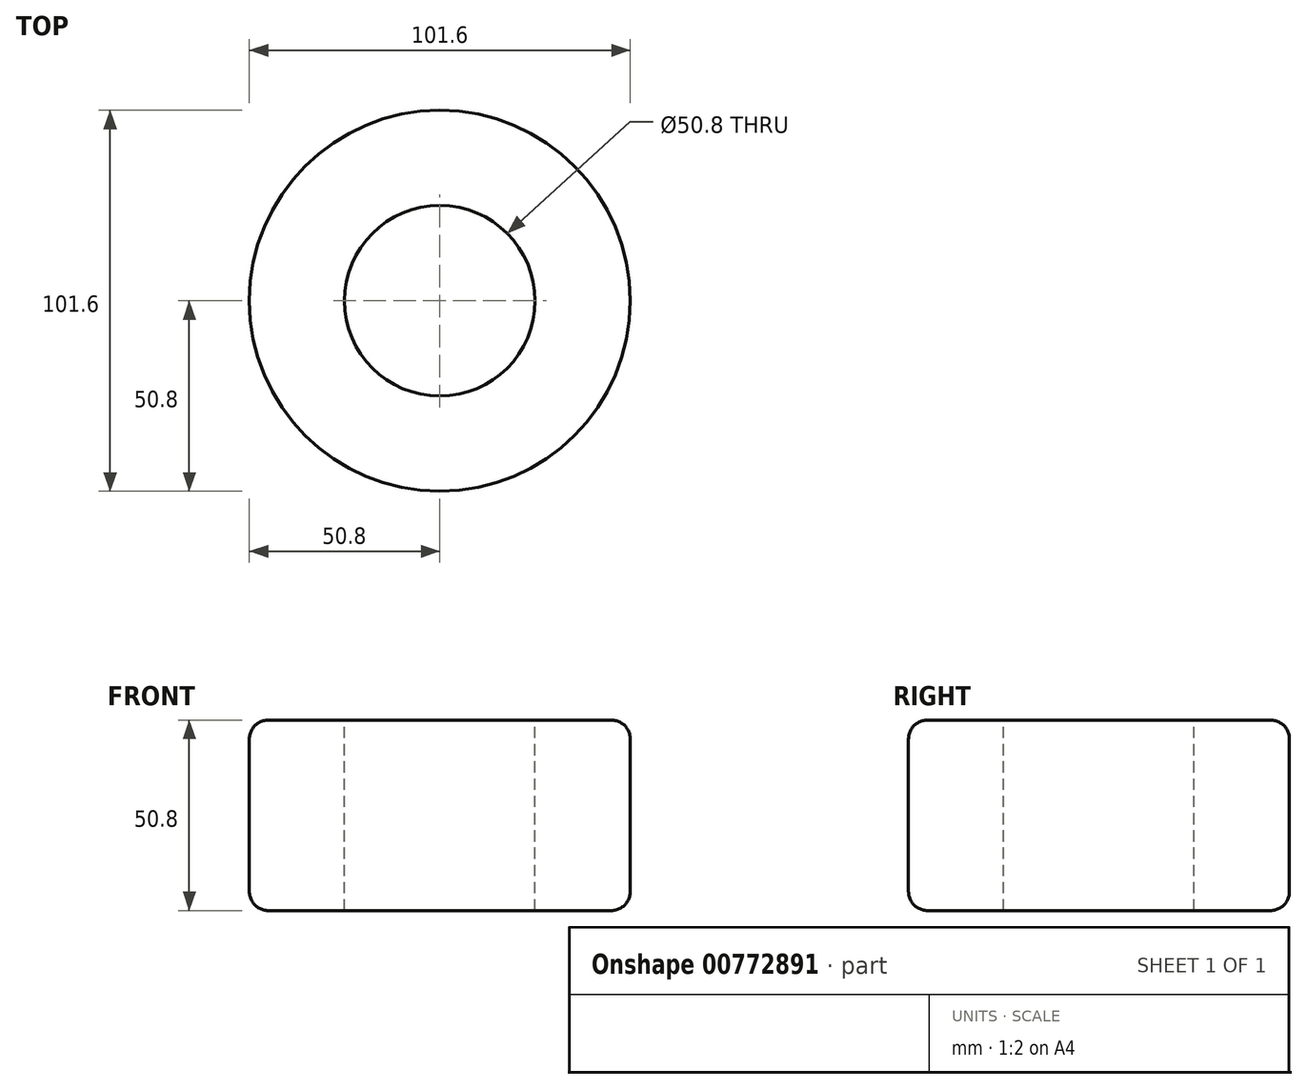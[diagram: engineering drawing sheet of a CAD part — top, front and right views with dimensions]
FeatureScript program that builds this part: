
annotation { "Feature Type Name" : "Feature", "Feature Type Description" : "" }
export const myFeature = defineFeature(function(context is Context, id is Id, definition is map)
    precondition{}
    {
        {
            var Q0;
            Q0=qCreatedBy(makeId("Top.planeOp"),FACE);
            var sketch = newSketch(context, id + "F0", { "sketchPlane" : qUnion([Q0])});
            skCircle(sketch, "E0", {"center": v(0, 0) * mm, "radius": 50.8 * mm});
            skSolve(sketch);
        }
        {
            var Q0;
            Q0=makeQuery(id+"F0.imprint","IMPRINT",FACE,{"disambiguationData":[TD([[makeQuery(id+"F0.imprint","IMPRINT",EDGE,{"derivedFrom":sQuery(id+"F0.wireOp",EDGE,"E0")}),1.0]])]});
            extrude(context, id + "F1", {"entities" : qUnion([Q0]), "oppositeDirection" : true, "depth" : 50.8 * mm, "offsetDistance" : 25.4 * mm});
        }
        {
            var Q0;
            Q0=qCreatedBy(makeId("Top.planeOp"),FACE);
            var sketch = newSketch(context, id + "F2", { "sketchPlane" : qUnion([Q0])});
            skCircle(sketch, "E1", {"center": v(0, 0) * mm, "radius": 25.4 * mm});
            skSolve(sketch);
        }
        {
            var Q0;
            Q0=makeQuery(id+"F2.imprint","IMPRINT",FACE,{"disambiguationData":[TD([[makeQuery(id+"F2.imprint","IMPRINT",EDGE,{"derivedFrom":sQuery(id+"F2.wireOp",EDGE,"E1")}),1.0]])]});
            extrude(context, id + "F3", {"entities" : qUnion([Q0]), "operationType" : NewBodyOperationType.REMOVE, "oppositeDirection" : true, "depth" : 50.8 * mm, "offsetDistance" : 25.4 * mm});
        }
        {
            var Q0;
            Q0=makeQuery(id+"F1.opExtrude","CAP_EDGE",EDGE,{"disambiguationData":[OSD([sQuery(id+"F0.wireOp",EDGE,"E0")])],"isStart":true});
            var Q1;
            Q1=makeQuery(id+"F3.boolean.opBoolean","COPY",EDGE,{"derivedFrom":makeQuery(id+"F3.opExtrude","CAP_EDGE",EDGE,{"disambiguationData":[OSD([sQuery(id+"F2.wireOp",EDGE,"E1")])],"isStart":true})});
            fillet(context, id + "F4", {"entities" : qUnion([Q0, Q1]), "radius" : 5.08 * mm, "tangentPropagation" : true, "allowEdgeOverflow" : false});
        }
        {
            var Q0;
            Q0=makeQuery(id+"F1.opExtrude","CAP_EDGE",EDGE,{"disambiguationData":[OSD([sQuery(id+"F0.wireOp",EDGE,"E0")])],"isStart":false});
            var Q1;
            Q1=makeQuery(id+"F3.boolean.opBoolean","COPY",EDGE,{"derivedFrom":makeQuery(id+"F3.opExtrude","CAP_EDGE",EDGE,{"disambiguationData":[OSD([sQuery(id+"F2.wireOp",EDGE,"E1")])],"isStart":false})});
            fillet(context, id + "F5", {"entities" : qUnion([Q0, Q1]), "radius" : 5.08 * mm, "tangentPropagation" : true, "allowEdgeOverflow" : false});
        }
    });
